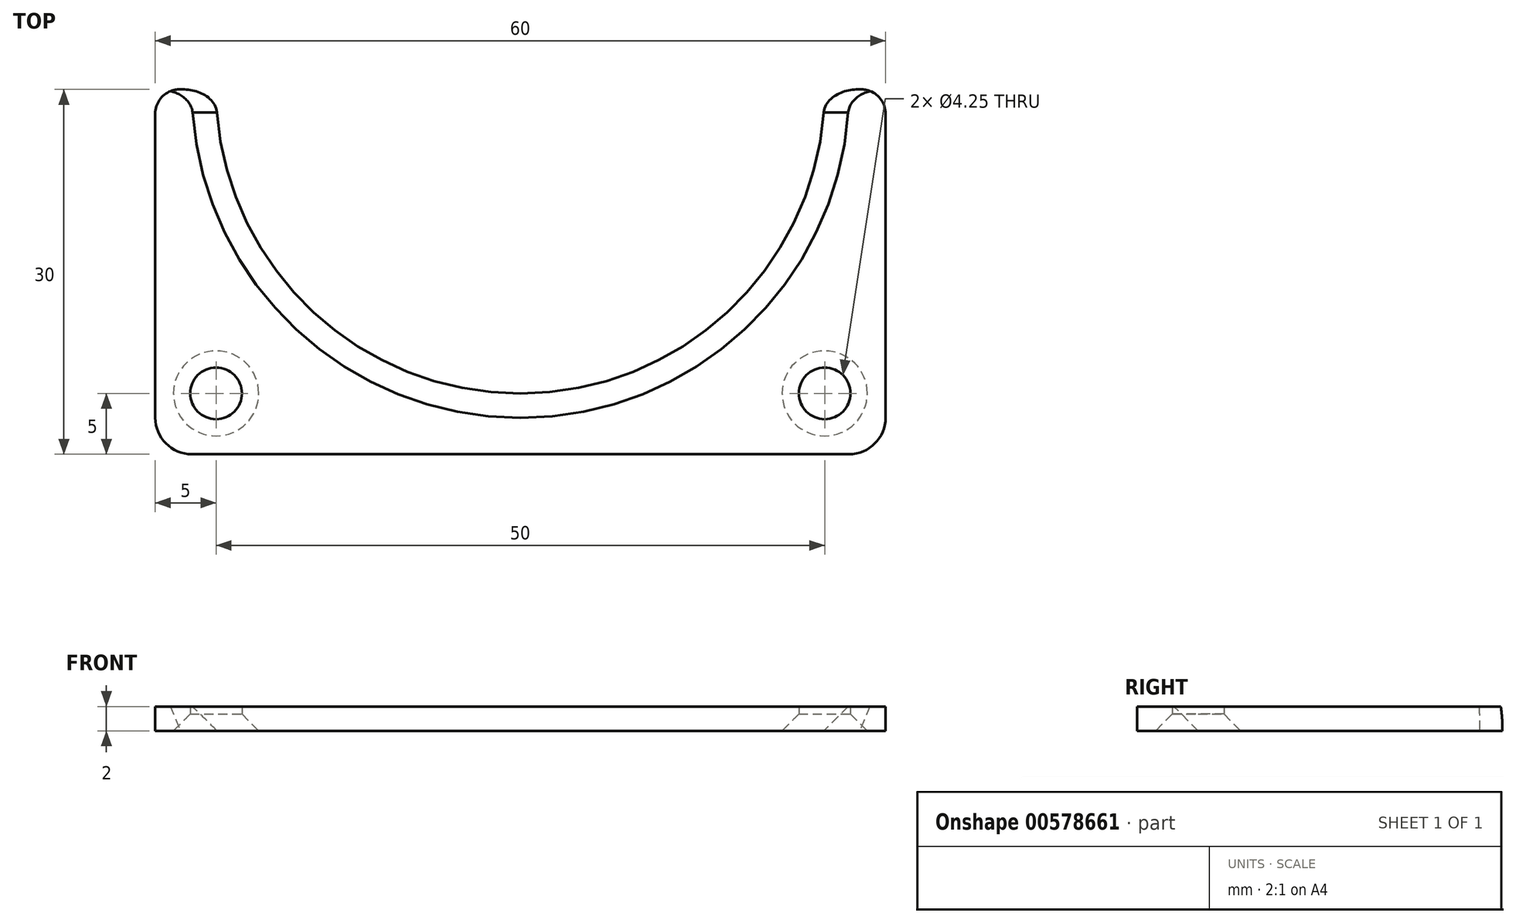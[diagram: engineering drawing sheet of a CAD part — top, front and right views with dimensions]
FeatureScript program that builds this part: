
annotation { "Feature Type Name" : "Feature", "Feature Type Description" : "" }
export const myFeature = defineFeature(function(context is Context, id is Id, definition is map)
    precondition{}
    {
        {
            var Q0;
            Q0=qCreatedBy(makeId("Top.planeOp"),FACE);
            var sketch = newSketch(context, id + "F0", { "sketchPlane" : qUnion([Q0])});
            skLineSegment(sketch, "E0.bottom", {"start": v(30, -15) * mm, "end": v(-30, -15) * mm});
            skLineSegment(sketch, "E0.top", {"start": v(30, 15) * mm, "end": v(-30, 15) * mm});
            skLineSegment(sketch, "E0.left", {"start": v(30, -15) * mm, "end": v(30, 15) * mm});
            skLineSegment(sketch, "E0.right", {"start": v(-30, -15) * mm, "end": v(-30, 15) * mm});
            skPoint(sketch, "E0.middle", {"position": v(0, 0) * mm});
            skPoint(sketch, "E1", {"position": v(-25, -10) * mm});
            skPoint(sketch, "E2", {"position": v(25, -10) * mm});
            skArc(sketch, "E3", {"start": v(-25, 15) * mm, "mid": v(0, -10) * mm, "end": v(25, 15) * mm});
            skSolve(sketch);
        }
        {
            var Q0;
            Q0=makeQuery(id+"F0.imprint","IMPRINT",FACE,{"disambiguationData":[TD([[makeQuery(id+"F0.imprint","IMPRINT",EDGE,{"derivedFrom":sQuery(id+"F0.wireOp",EDGE,"E0.bottom")}),-1.0]])]});
            extrude(context, id + "F1", {"entities" : qUnion([Q0]), "depth" : 2 * mm, "offsetDistance" : 25 * mm});
        }
        {
            var Q0;
            Q0=sQuery(id+"F0.wireOp",VERTEX,"E1");
            var Q1;
            Q1=sQuery(id+"F0.wireOp",VERTEX,"E2");
            var Q2;
            Q2=makeQuery(id+"F1.opExtrude","SWEPT_BODY",BODY,{"disambiguationData":[OSD([sQuery(id+"F0.wireOp",EDGE,"E0.bottom"),sQuery(id+"F0.wireOp",EDGE,"E0.top"),sQuery(id+"F0.wireOp",EDGE,"E0.left"),sQuery(id+"F0.wireOp",EDGE,"E0.right"),sQuery(id+"F0.wireOp",EDGE,"E3")])]});
            hole(context, id + "F2", {"style" : HoleStyle.C_SINK, "endStyle" : HoleEndStyle.BLIND, "oppositeDirection" : true, "holeDiameter" : 4.25 * mm, "cSinkDiameter" : 7 * mm, "cSinkAngle" : 90 * degree, "majorDiameter" : 5 * mm, "holeDepth" : 15 * mm, "isTappedThrough" : true, "tappedDepth" : 12 * mm, "tapClearance" : 3, "locations" : qUnion([Q0, Q1]), "scope" : qUnion([Q2])});
        }
        {
            var Q0;
            Q0=makeQuery(id+"F1.opExtrude","SWEPT_EDGE",EDGE,{"disambiguationData":[OSD([sQuery(id+"F0.wireOp",EDGE,"E0.bottom"),sQuery(id+"F0.wireOp",EDGE,"E0.right")])]});
            var Q1;
            Q1=makeQuery(id+"F1.opExtrude","SWEPT_EDGE",EDGE,{"disambiguationData":[OSD([sQuery(id+"F0.wireOp",EDGE,"E0.bottom"),sQuery(id+"F0.wireOp",EDGE,"E0.left")])]});
            fillet(context, id + "F3", {"entities" : qUnion([Q0, Q1]), "radius" : 3 * mm, "tangentPropagation" : true, "allowEdgeOverflow" : false});
        }
        {
            var Q0;
            Q0=makeQuery(id+"F1.opExtrude","CAP_EDGE",EDGE,{"disambiguationData":[OSD([sQuery(id+"F0.wireOp",EDGE,"E3")])],"isStart":false});
            chamfer(context, id + "F4", {"entities" : qUnion([Q0]), "width" : 2 * mm, "tangentPropagation" : true});
        }
        {
            var Q0;
            {var subQ0=sQuery(id+"F0.wireOp",EDGE,"E0.top");var subQ1=sQuery(id+"F0.wireOp",EDGE,"E3");Q0=makeQuery(id+"F4.opChamfer","BLEND_EDGE",EDGE,{"blendedFrom":[makeQuery(id+"F1.opExtrude","CAP_EDGE",EDGE,{"disambiguationData":[OSD([subQ1])],"isStart":false}),makeQuery(id+"F1.opExtrude","SWEPT_FACE",FACE,{"disambiguationData":[OSD([subQ0]),TDD([makeQuery(id+"F0.imprint","IMPRINT",EDGE,{"disambiguationData":[TD([[makeQuery(id+"F0.imprint","INTERSECT",VERTEX,{"derivedFrom":[subQ0,sQuery(id+"F0.wireOp",EDGE,"E0.left")]}),-1.0]])],"derivedFrom":subQ0})])]})],"blendedInto":[makeQuery(id+"F1.opExtrude","SWEPT_FACE",FACE,{"disambiguationData":[OSD([subQ0]),TDD([makeQuery(id+"F0.imprint","IMPRINT",EDGE,{"disambiguationData":[TD([[makeQuery(id+"F0.imprint","INTERSECT",VERTEX,{"derivedFrom":[subQ0,sQuery(id+"F0.wireOp",EDGE,"E0.left")]}),-1.0]])],"derivedFrom":subQ0})])]})]});}
            var Q1;
            {var subQ0=sQuery(id+"F0.wireOp",EDGE,"E0.top");var subQ1=sQuery(id+"F0.wireOp",EDGE,"E3");Q1=makeQuery(id+"F4.opChamfer","BLEND_EDGE",EDGE,{"blendedFrom":[makeQuery(id+"F1.opExtrude","CAP_EDGE",EDGE,{"disambiguationData":[OSD([subQ1])],"isStart":false}),makeQuery(id+"F1.opExtrude","SWEPT_FACE",FACE,{"disambiguationData":[OSD([subQ0]),TDD([makeQuery(id+"F0.imprint","IMPRINT",EDGE,{"disambiguationData":[TD([[makeQuery(id+"F0.imprint","INTERSECT",VERTEX,{"derivedFrom":[subQ0,sQuery(id+"F0.wireOp",EDGE,"E0.right")]}),1.0]])],"derivedFrom":subQ0})])]})],"blendedInto":[makeQuery(id+"F1.opExtrude","SWEPT_FACE",FACE,{"disambiguationData":[OSD([subQ0]),TDD([makeQuery(id+"F0.imprint","IMPRINT",EDGE,{"disambiguationData":[TD([[makeQuery(id+"F0.imprint","INTERSECT",VERTEX,{"derivedFrom":[subQ0,sQuery(id+"F0.wireOp",EDGE,"E0.right")]}),1.0]])],"derivedFrom":subQ0})])]})]});}
            var Q2;
            Q2=makeQuery(id+"F1.opExtrude","SWEPT_EDGE",EDGE,{"disambiguationData":[OSD([sQuery(id+"F0.wireOp",EDGE,"E0.top"),sQuery(id+"F0.wireOp",EDGE,"E0.right")])]});
            var Q3;
            Q3=makeQuery(id+"F1.opExtrude","SWEPT_EDGE",EDGE,{"disambiguationData":[OSD([sQuery(id+"F0.wireOp",EDGE,"E0.top"),sQuery(id+"F0.wireOp",EDGE,"E0.left")])]});
            fillet(context, id + "F5", {"entities" : qUnion([Q0, Q1, Q2, Q3]), "radius" : 2 * mm, "tangentPropagation" : true, "allowEdgeOverflow" : false});
        }
    });
